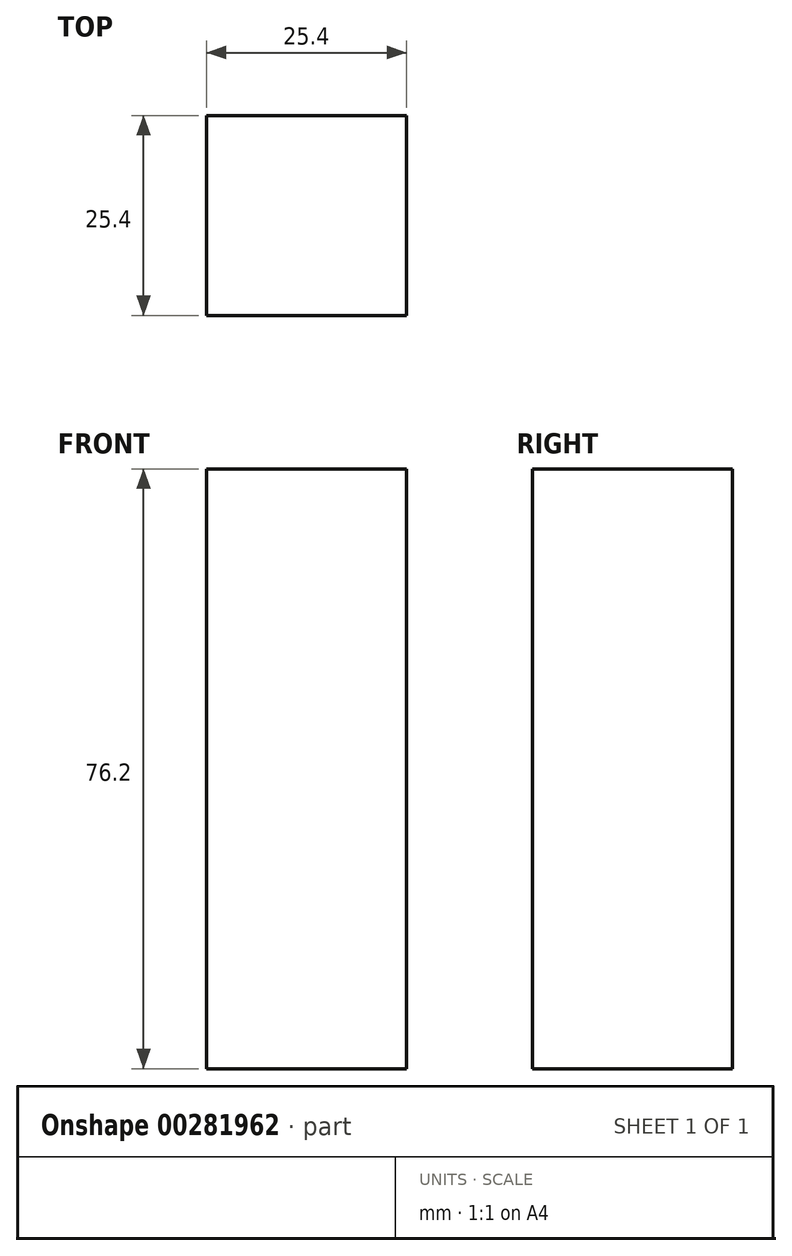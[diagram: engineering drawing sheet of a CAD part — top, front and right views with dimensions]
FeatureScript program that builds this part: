
annotation { "Feature Type Name" : "Feature", "Feature Type Description" : "" }
export const myFeature = defineFeature(function(context is Context, id is Id, definition is map)
    precondition{}
    {
        {
            var Q0;
            Q0=qCreatedBy(makeId("Front.planeOp"),FACE);
            var sketch = newSketch(context, id + "F0", { "sketchPlane" : qUnion([Q0])});
            skLineSegment(sketch, "E0.bottom", {"start": v(21.2, 0) * mm, "end": v(-4.2, 0) * mm});
            skLineSegment(sketch, "E0.top", {"start": v(21.2, 76.2) * mm, "end": v(-4.2, 76.2) * mm});
            skLineSegment(sketch, "E0.left", {"start": v(21.2, 0) * mm, "end": v(21.2, 76.2) * mm});
            skLineSegment(sketch, "E0.right", {"start": v(-4.2, 0) * mm, "end": v(-4.2, 76.2) * mm});
            skSolve(sketch);
        }
        {
            var Q0;
            Q0 = qSketchRegion(id + "F0", true);
            extrude(context, id + "F1", {"entities" : qUnion([Q0]), "depth" : 25.4 * mm});
        }
    });
